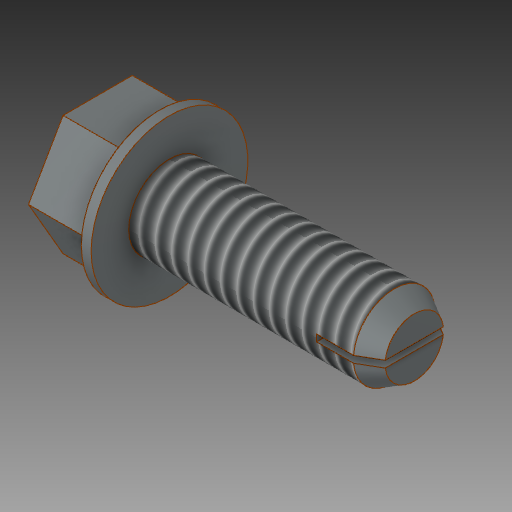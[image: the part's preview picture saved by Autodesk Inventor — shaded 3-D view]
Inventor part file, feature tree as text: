
AUTODESK INVENTOR PART (.ipt)
format: ipt  version: 2017.1 (Build 211199000, 199)  size: 183,296 bytes
history: native  units: in
note: dims shown in document units (in); Inventor stores cm internally (conversion verified against a paired STEP export)
features: thread x1, other x1
ambient origin geometry x8: Origin, YZ Plane, XZ Plane, XY Plane, X Axis, Y Axis, Z Axis, Center Point
bodies: Solid1 (feature_tree)
feature tree (2):
  thread  "Thread1"  [1 undecoded]
  other  "point_Cut-Extrude10"
note: 1 required parameter value undecoded (feature->parameter linkage not recoverable at this tier; creation-order binding heuristic only, values carry confidence <= 0.55)
